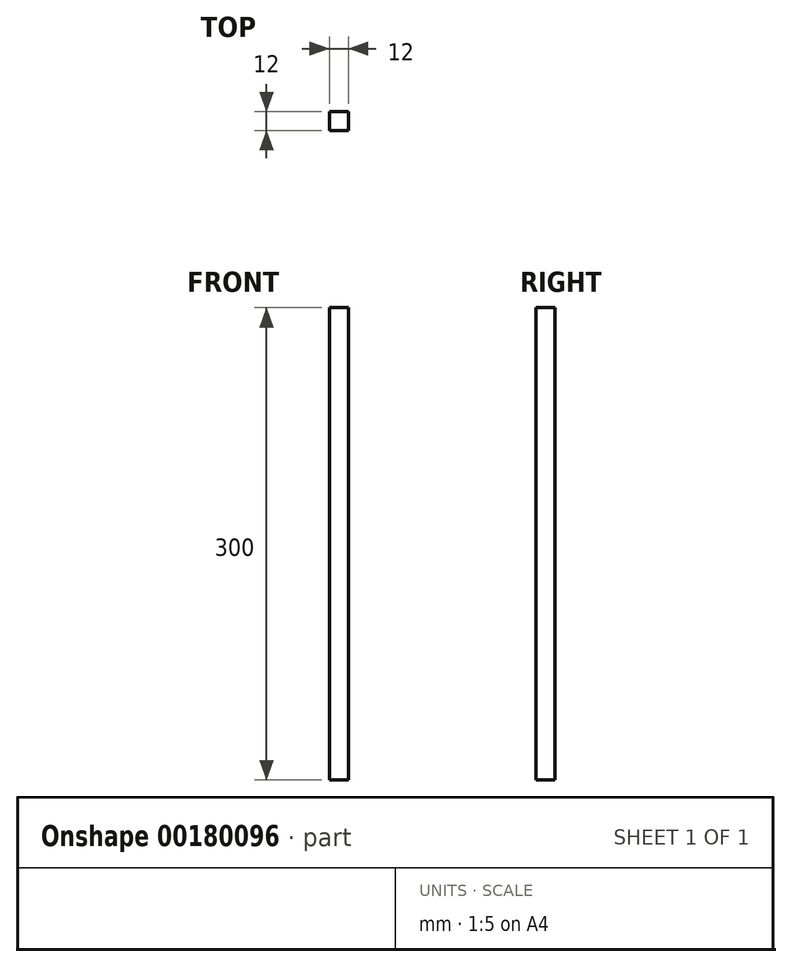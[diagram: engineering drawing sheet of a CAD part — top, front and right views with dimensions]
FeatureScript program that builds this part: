
annotation { "Feature Type Name" : "Feature", "Feature Type Description" : "" }
export const myFeature = defineFeature(function(context is Context, id is Id, definition is map)
    precondition{}
    {
        {
            var Q0;
            Q0=qCreatedBy(makeId("Top.planeOp"),FACE);
            var sketch = newSketch(context, id + "F0", { "sketchPlane" : qUnion([Q0])});
            skLineSegment(sketch, "E0.bottom", {"start": v(6, -6) * mm, "end": v(-6, -6) * mm});
            skLineSegment(sketch, "E0.top", {"start": v(6, 6) * mm, "end": v(-6, 6) * mm});
            skLineSegment(sketch, "E0.left", {"start": v(6, -6) * mm, "end": v(6, 6) * mm});
            skLineSegment(sketch, "E0.right", {"start": v(-6, -6) * mm, "end": v(-6, 6) * mm});
            skPoint(sketch, "E0.middle", {"position": v(0, 0) * mm});
            skSolve(sketch);
        }
        {
            var Q0;
            Q0 = qSketchRegion(id + "F0", true);
            extrude(context, id + "F1", {"entities" : qUnion([Q0]), "depth" : 300 * mm});
        }
    });
